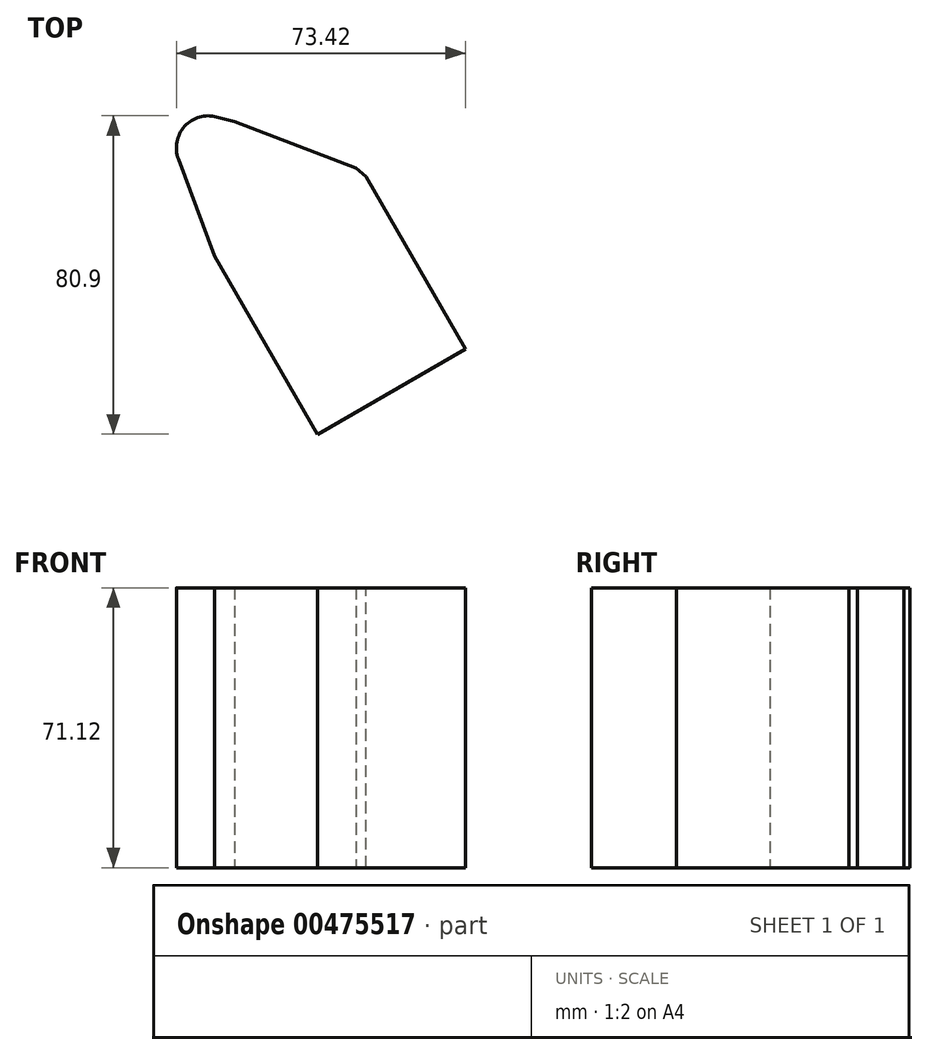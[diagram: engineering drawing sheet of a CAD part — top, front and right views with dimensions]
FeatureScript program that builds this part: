
annotation { "Feature Type Name" : "Feature", "Feature Type Description" : "" }
export const myFeature = defineFeature(function(context is Context, id is Id, definition is map)
    precondition{}
    {
        {
            var Q0;
            Q0=qCreatedBy(makeId("Top.planeOp"),FACE);
            var sketch = newSketch(context, id + "F0", { "sketchPlane" : qUnion([Q0])});
            skLineSegment(sketch, "E0", {"start": v(-12.3, 22.6) * mm, "end": v(7.5, 17.29) * mm});
            skLineSegment(sketch, "E1", {"start": v(40, 4.85) * mm, "end": v(7.5, 17.29) * mm});
            skLineSegment(sketch, "E2", {"start": v(2.47, -16.82) * mm, "end": v(-12.3, 22.6) * mm});
            skLineSegment(sketch, "E3", {"start": v(2.47, -16.82) * mm, "end": v(40, 4.85) * mm});
            skSolve(sketch);
        }
        {
            var Q0;
            Q0=makeQuery(id+"F0.imprint","IMPRINT",FACE,{"disambiguationData":[TD([[makeQuery(id+"F0.imprint","IMPRINT",EDGE,{"derivedFrom":sQuery(id+"F0.wireOp",EDGE,"E0")}),-1.0]])]});
            extrude(context, id + "F1", {"entities" : qUnion([Q0]), "depth" : 71.12 * mm});
        }
        {
            var Q0;
            Q0=makeQuery(id+"F1.opExtrude","SWEPT_FACE",FACE,{"disambiguationData":[OSD([sQuery(id+"F0.wireOp",EDGE,"E3")])]});
            extrude(context, id + "F2", {"entities" : qUnion([Q0]), "operationType" : NewBodyOperationType.ADD, "depth" : 52.32 * mm});
        }
        {
            var Q0;
            {var subQ0=sQuery(id+"F0.wireOp",EDGE,"E3");var subQ1=sQuery(id+"F0.wireOp",EDGE,"E1");Q0=makeQuery(id+"F2.boolean.opBoolean","MERGE",EDGE,{"derivedFrom":[makeQuery(id+"F1.opExtrude","SWEPT_EDGE",EDGE,{"disambiguationData":[OSD([subQ1,subQ0])]}),makeQuery(id+"F2.opExtrude","CAP_EDGE",EDGE,{"disambiguationData":[OSD([subQ1,subQ0])],"isStart":true})]});}
            chamfer(context, id + "F3", {"entities" : qUnion([Q0]), "width" : 5.08 * mm, "tangentPropagation" : true});
        }
        {
            var Q0;
            Q0=makeQuery(id+"F1.opExtrude","SWEPT_EDGE",EDGE,{"disambiguationData":[OSD([sQuery(id+"F0.wireOp",EDGE,"E0"),sQuery(id+"F0.wireOp",EDGE,"E2")])]});
            fillet(context, id + "F4", {"entities" : qUnion([Q0]), "radius" : 8.14 * mm, "tangentPropagation" : true, "allowEdgeOverflow" : false});
        }
    });
